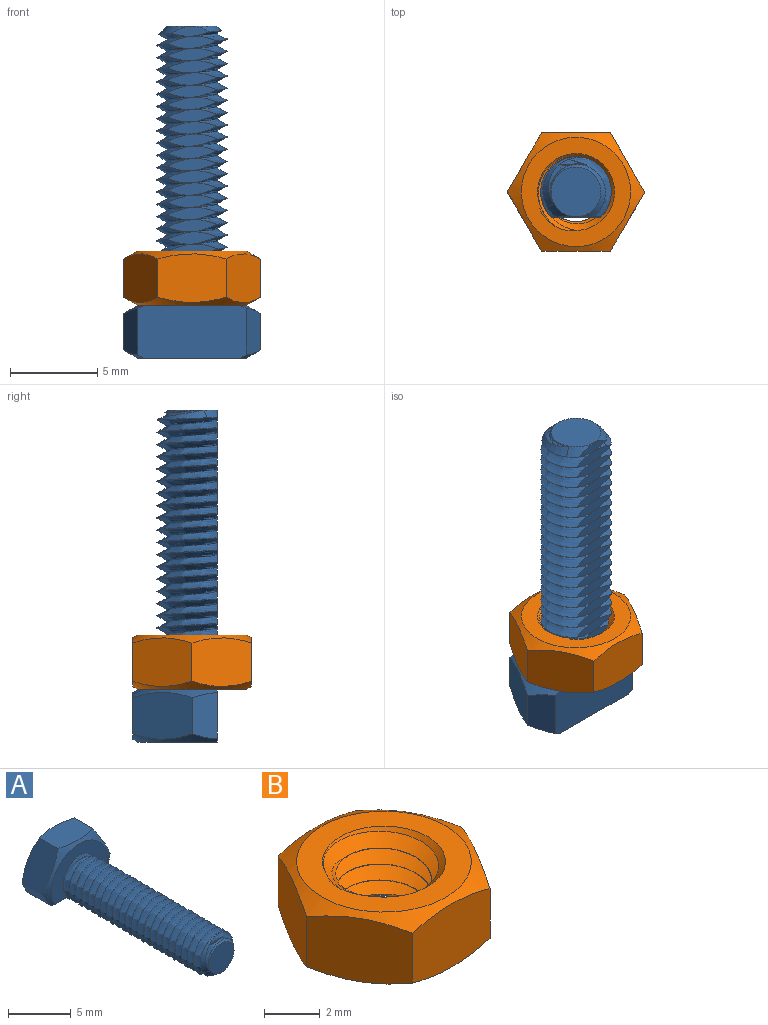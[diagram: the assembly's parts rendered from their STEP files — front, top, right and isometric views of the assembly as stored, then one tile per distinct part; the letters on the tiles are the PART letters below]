
ASSEMBLY  parts=2 mates=1
PART A: 61 faces, bbox 8.3x19.9x6.7 mm
  f0: plane 6.74x5.05mm, normal (0,-1,0), area 14.5mm2, adj f22,f26,f27,f28,f37
  f1: cylinder r=2.02mm len=4.04mm, axis (0,1,0), area 0.1mm2, adj f26,f27,f58,f59
  f2: cylinder r=2.02mm len=4.04mm, axis (0,1,0), area 0.1mm2, adj f26,f27,f57,f58
  f3: cylinder r=2.02mm len=4.04mm, axis (0,1,0), area 0.1mm2, adj f26,f27,f56,f57
  f4: cylinder r=2.02mm len=4.04mm, axis (0,1,0), area 0.1mm2, adj f26,f27,f55,f56
  f5: cylinder r=2.02mm len=4.04mm, axis (0,1,0), area 0.1mm2, adj f26,f27,f54,f55
  f6: cylinder r=2.02mm len=4.04mm, axis (0,1,0), area 0.1mm2, adj f26,f27,f53,f54
  f7: cylinder r=2.02mm len=4.04mm, axis (0,1,0), area 0.1mm2, adj f26,f27,f52,f53
  f8: cylinder r=2.02mm len=4.04mm, axis (0,1,0), area 0.1mm2, adj f26,f27,f51,f52
  f9: cylinder r=2.02mm len=4.04mm, axis (0,1,0), area 0.1mm2, adj f26,f27,f50,f51
  f10: cylinder r=2.02mm len=4.04mm, axis (0,1,0), area 0.1mm2, adj f26,f27,f49,f50
  f11: cylinder r=2.02mm len=4.04mm, axis (0,1,0), area 0.1mm2, adj f26,f27,f48,f49
  f12: cylinder r=2.02mm len=4.04mm, axis (0,1,0), area 0.1mm2, adj f26,f27,f47,f48
  f13: cylinder r=2.02mm len=4.04mm, axis (0,1,0), area 0.1mm2, adj f26,f27,f46,f47
  f14: cylinder r=2.02mm len=4.04mm, axis (0,1,0), area 0.1mm2, adj f26,f27,f45,f46
  f15: cylinder r=2.02mm len=4.04mm, axis (0,1,0), area 0.1mm2, adj f26,f27,f44,f45
  f16: cylinder r=2.02mm len=4.04mm, axis (0,1,0), area 0.1mm2, adj f26,f27,f43,f44
  f17: cylinder r=2.02mm len=4.04mm, axis (0,1,0), area 0.1mm2, adj f26,f27,f42,f43
  f18: cylinder r=2.02mm len=4.04mm, axis (0,1,0), area 0.1mm2, adj f26,f27,f41,f42
  f19: cylinder r=2.02mm len=4.04mm, axis (0,1,0), area 0.1mm2, adj f26,f27,f40,f41
  f20: cylinder r=2.02mm len=4.04mm, axis (0,1,0), area 0.1mm2, adj f26,f27,f39,f40
  f21: cylinder r=2.02mm len=4.04mm, axis (0,1,0), area 0.1mm2, adj f26,f27,f38,f39
  f22: cylinder r=2.02mm len=3.45mm, axis (0,1,0), area 0.1mm2, adj f0,f26,f27,f38
  f23: cylinder r=2.02mm len=3.44mm, axis (0,1,0), area 0mm2, adj f25,f26,f27,f59
  f24: cone r=1.42mm half-angle=45deg, axis (0,1,0), area 2.4mm2, adj f25,f26,f33,f60
  f25: cone r=1.42mm half-angle=45deg, axis (0,1,0), area 1.3mm2, adj f23,f24,f26,f27
  f26: bspline ~16.8x4.67mm, area 138.1mm2, adj f0,f1,f2,f3,f4,f5,f6,f7
  f27: bspline ~16.45x4.67mm, area 137.9mm2, adj f0,f1,f2,f3,f4,f5,f6,f7
  f28: cone r=3.13mm half-angle=60deg, axis (0,1,0), area 7.3mm2, adj f0,f29,f30,f34,f35,f36,f37
  f29: plane 2.9x1.66mm, normal (-0.87,0,-0.5), area 4mm2, adj f28,f31,f34,f37
  f30: plane 2.9x1.66mm, normal (0.87,0,-0.5), area 4mm2, adj f28,f31,f36,f37
  f31: cone r=3.13mm half-angle=60deg, axis (0,-1,0), area 7.3mm2, adj f29,f30,f32,f34,f35,f36,f37
  f32: plane 6.25x4.56mm, normal (0,1,0), area 24mm2, adj f31,f37
  f33: plane 2.84x2.84mm, normal (0,-1,0), area 6.3mm2, adj f24
  f34: plane 3.4x2.69mm, normal (-0.87,0,0.5), area 9.7mm2, adj f28,f29,f31,f35
  f35: plane 3.93x2.69mm, normal (0,0,1), area 9.7mm2, adj f28,f31,f34,f36
  f36: plane 3.4x2.69mm, normal (0.87,0,0.5), area 9.7mm2, adj f28,f30,f31,f35
  f37: plane 6.29x3.11mm, normal (0,0,-1), area 18.5mm2, adj f0,f27,f28,f29,f30,f31,f32
  f38: plane 2.85x0.71mm, normal (0,0,-1), area 1.3mm2, adj f21,f22,f26,f27
  f39: plane 2.85x0.71mm, normal (0,0,-1), area 1.3mm2, adj f20,f21,f26,f27
  f40: plane 2.85x0.71mm, normal (0,0,-1), area 1.3mm2, adj f19,f20,f26,f27
  f41: plane 2.85x0.71mm, normal (0,0,-1), area 1.3mm2, adj f18,f19,f26,f27
  f42: plane 2.85x0.71mm, normal (0,0,-1), area 1.3mm2, adj f17,f18,f26,f27
  f43: plane 2.85x0.71mm, normal (0,0,-1), area 1.3mm2, adj f16,f17,f26,f27
  f44: plane 2.85x0.71mm, normal (0,0,-1), area 1.3mm2, adj f15,f16,f26,f27
  f45: plane 2.85x0.71mm, normal (0,0,-1), area 1.3mm2, adj f14,f15,f26,f27
  f46: plane 2.85x0.71mm, normal (0,0,-1), area 1.3mm2, adj f13,f14,f26,f27
  f47: plane 2.85x0.71mm, normal (0,0,-1), area 1.3mm2, adj f12,f13,f26,f27
  f48: plane 2.85x0.71mm, normal (0,0,-1), area 1.3mm2, adj f11,f12,f26,f27
  f49: plane 2.85x0.71mm, normal (0,0,-1), area 1.3mm2, adj f10,f11,f26,f27
  f50: plane 2.85x0.71mm, normal (0,0,-1), area 1.3mm2, adj f9,f10,f26,f27
  f51: plane 2.85x0.71mm, normal (0,0,-1), area 1.3mm2, adj f8,f9,f26,f27
  f52: plane 2.85x0.71mm, normal (0,0,-1), area 1.3mm2, adj f7,f8,f26,f27
  f53: plane 2.85x0.71mm, normal (0,0,-1), area 1.3mm2, adj f6,f7,f26,f27
  f54: plane 2.85x0.71mm, normal (0,0,-1), area 1.3mm2, adj f5,f6,f26,f27
  f55: plane 2.85x0.71mm, normal (0,0,-1), area 1.3mm2, adj f4,f5,f26,f27
  f56: plane 2.85x0.71mm, normal (0,0,-1), area 1.3mm2, adj f3,f4,f26,f27
  f57: plane 2.85x0.71mm, normal (0,0,-1), area 1.3mm2, adj f2,f3,f26,f27
  f58: plane 2.85x0.71mm, normal (0,0,-1), area 1.3mm2, adj f1,f2,f26,f27
  f59: plane 2.85x0.71mm, normal (0,0,-1), area 1.3mm2, adj f1,f23,f26,f27
  f60: plane 2.16x0.58mm, normal (0,0,-1), area 0.8mm2, adj f24,f26
PART B: 15 faces, bbox 7.9x7.9x4 mm
  f0: plane 6.28x6.28mm, normal (0,0,-1), area 15.4mm2, adj f4,f11,f13,f14
  f1: plane 6.27x6.27mm, normal (0,0,1), area 15.4mm2, adj f3,f12,f13,f14
  f2: cylinder r=1.7mm len=3.4mm, axis (0,0,1), area 0.3mm2, adj f11,f12,f13,f14
  f3: cone r=4.97mm half-angle=60deg, axis (0,0,-1), area 10.8mm2, adj f1,f5,f6,f7,f8,f9,f10
  f4: cone r=4.97mm half-angle=60deg, axis (0,0,1), area 10.8mm2, adj f0,f5,f6,f7,f8,f9,f10
  f5: plane 3.4x2.79mm, normal (-0.87,-0.5,0), area 10.1mm2, adj f3,f4,f6,f10
  f6: plane 3.4x2.79mm, normal (-0.87,0.5,0), area 10.1mm2, adj f3,f4,f5,f7
  f7: plane 3.93x2.79mm, normal (0,1,0), area 10.1mm2, adj f3,f4,f6,f8
  f8: plane 3.4x2.79mm, normal (0.87,0.5,0), area 10.1mm2, adj f3,f4,f7,f9
  f9: plane 3.4x2.79mm, normal (0.87,-0.5,0), area 10.1mm2, adj f3,f4,f8,f10
  f10: plane 3.93x2.79mm, normal (0,-1,0), area 10.1mm2, adj f3,f4,f5,f9
  f11: cone r=2.2mm half-angle=45deg, axis (0,0,-1), area 3.8mm2, adj f0,f2,f13,f14
  f12: cone r=1.7mm half-angle=45deg, axis (0,0,1), area 3.8mm2, adj f1,f2,f13,f14
  f13: bspline ~5.31x4.6mm, area 33.6mm2, adj f0,f1,f2,f11,f12,f14
  f14: bspline ~5.31x4.6mm, area 33.6mm2, adj f0,f1,f2,f11,f12,f13
PLACE A rot(axis=(-1,0,0),90deg) t=(-9.48,-1.88,-8.28)mm
PLACE B rot(axis=(0,0,1),59.9deg) t=(-24.5,-12,-3.66)mm
MATE cylindrical A.f1 <-> B.f0  axis (0,0,1) through (-19.48,-3.37,9.22)mm
